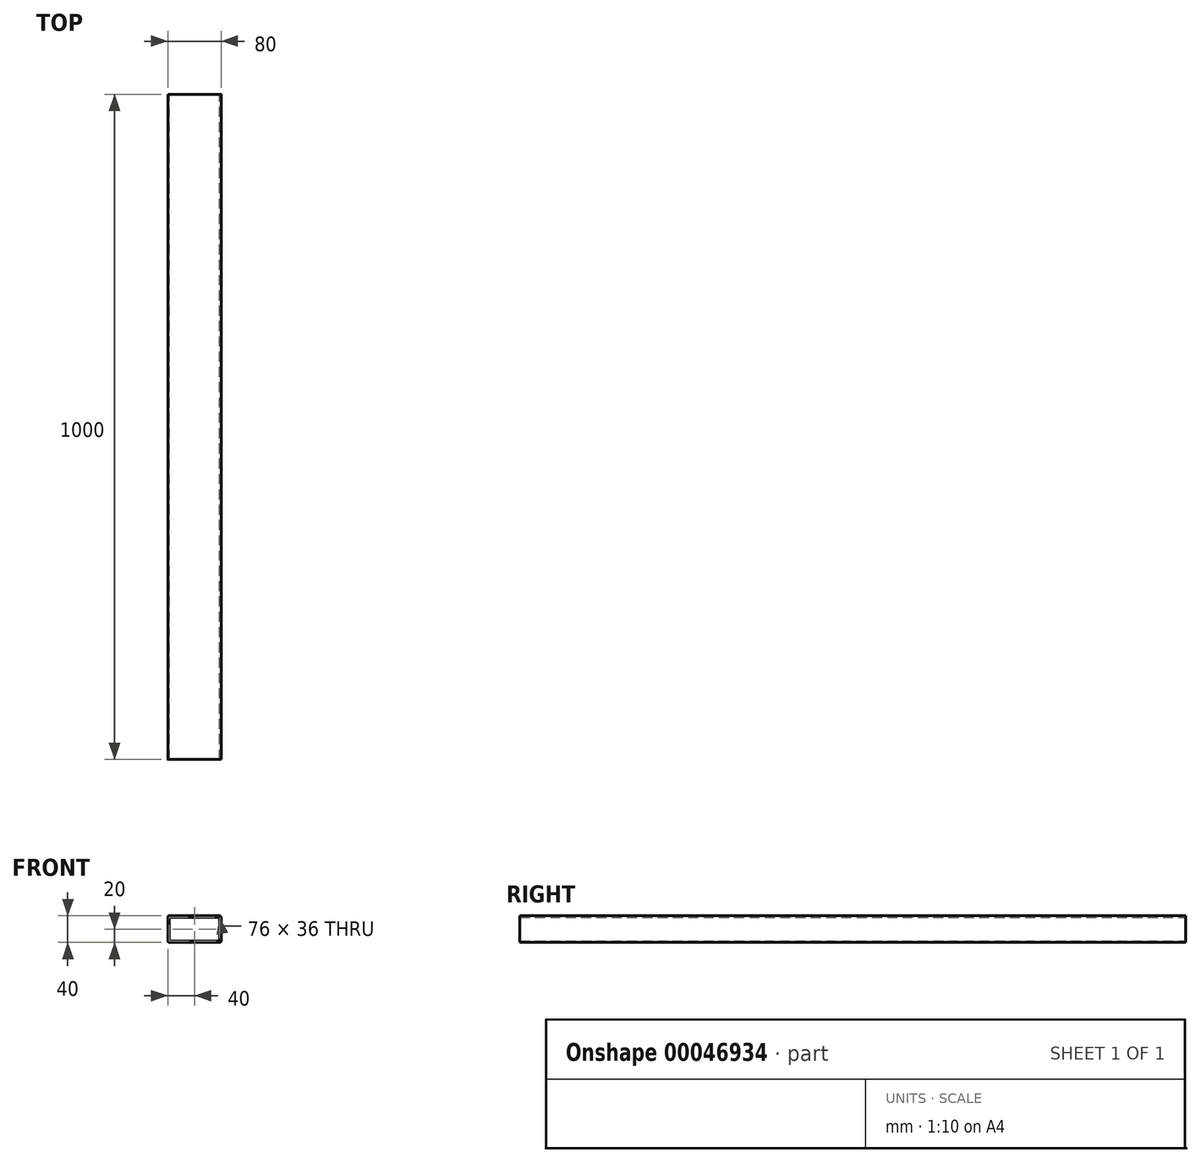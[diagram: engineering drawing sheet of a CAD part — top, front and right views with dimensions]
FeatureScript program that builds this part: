
annotation { "Feature Type Name" : "Feature", "Feature Type Description" : "" }
export const myFeature = defineFeature(function(context is Context, id is Id, definition is map)
    precondition{}
    {
        {
            var Q0;
            Q0=qCreatedBy(makeId("Front.planeOp"),FACE);
            var sketch = newSketch(context, id + "F0", { "sketchPlane" : qUnion([Q0])});
            skLineSegment(sketch, "E0", {"start": v(38, 18) * mm, "end": v(38, -18) * mm});
            skLineSegment(sketch, "E1", {"start": v(-38, 18) * mm, "end": v(38, 18) * mm});
            skLineSegment(sketch, "E2", {"start": v(-38, -18) * mm, "end": v(-38, 18) * mm});
            skLineSegment(sketch, "E3", {"start": v(38, -18) * mm, "end": v(-38, -18) * mm});
            skLineSegment(sketch, "E4", {"start": v(-40, 18) * mm, "end": v(-40, -18) * mm});
            skArc(sketch, "E5", {"start": v(-38, 20) * mm, "mid": v(-39.41, 19.41) * mm, "end": v(-40, 18) * mm});
            skLineSegment(sketch, "E6", {"start": v(38, 20) * mm, "end": v(-38, 20) * mm});
            skArc(sketch, "E7", {"start": v(40, 18) * mm, "mid": v(39.41, 19.41) * mm, "end": v(38, 20) * mm});
            skLineSegment(sketch, "E8", {"start": v(40, -18) * mm, "end": v(40, 18) * mm});
            skArc(sketch, "E9", {"start": v(38, -20) * mm, "mid": v(39.41, -19.41) * mm, "end": v(40, -18) * mm});
            skLineSegment(sketch, "E10", {"start": v(-38, -20) * mm, "end": v(38, -20) * mm});
            skArc(sketch, "E11", {"start": v(-40, -18) * mm, "mid": v(-39.41, -19.41) * mm, "end": v(-38, -20) * mm});
            skSolve(sketch);
        }
        {
            var Q0;
            Q0=qSketchRegion(id+"F0",true);
            extrude(context, id + "F1", {"entities" : qUnion([Q0]), "depth" : 1000 * mm});
        }
    });
